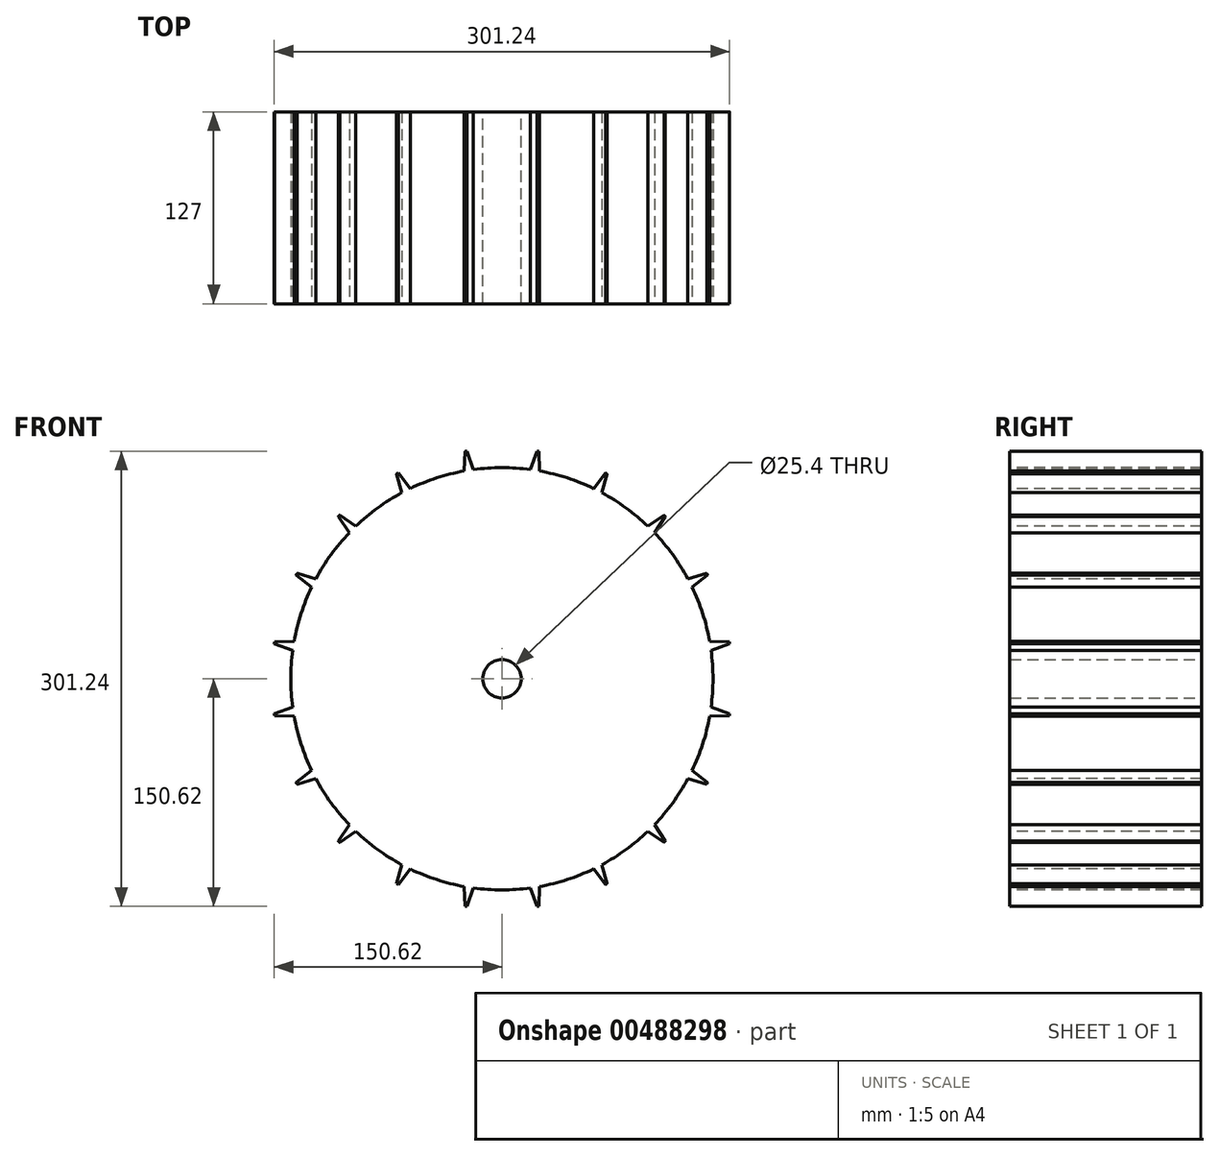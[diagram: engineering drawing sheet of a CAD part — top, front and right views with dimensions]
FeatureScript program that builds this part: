
annotation { "Feature Type Name" : "Feature", "Feature Type Description" : "" }
export const myFeature = defineFeature(function(context is Context, id is Id, definition is map)
    precondition{}
    {
        {
            var Q0;
            Q0=qCreatedBy(makeId("Front.planeOp"),FACE);
            var sketch = newSketch(context, id + "F0", { "sketchPlane" : qUnion([Q0])});
            skCircle(sketch, "E0", {"center": v(0, 0) * mm, "radius": 152.4 * mm});
            skCircle(sketch, "E1", {"center": v(0, 0) * mm, "radius": 76.2 * mm});
            skCircle(sketch, "E2", {"center": v(0, 0) * mm, "radius": 12.7 * mm});
            skSolve(sketch);
        }
        {
            var Q0;
            Q0=makeQuery(id+"F0.imprint","IMPRINT",FACE,{"disambiguationData":[TD([[makeQuery(id+"F0.imprint","IMPRINT",EDGE,{"derivedFrom":sQuery(id+"F0.wireOp",EDGE,"E0")}),1.0]])]});
            var Q1;
            Q1=makeQuery(id+"F0.imprint","IMPRINT",FACE,{"disambiguationData":[TD([[makeQuery(id+"F0.imprint","IMPRINT",EDGE,{"derivedFrom":sQuery(id+"F0.wireOp",EDGE,"E1")}),1.0]])]});
            extrude(context, id + "F1", {"entities" : qUnion([Q0, Q1]), "endBound" : BoundingType.SYMMETRIC, "depth" : 127 * mm});
        }
        {
            var Q0;
            Q0=qCreatedBy(makeId("Front.planeOp"),FACE);
            var sketch = newSketch(context, id + "F2", { "sketchPlane" : qUnion([Q0])});
            skLineSegment(sketch, "E3", {"start": v(0, 0) * mm, "end": v(0, 208.27) * mm, "construction": true});
            skArc(sketch, "E4", {"start": v(18.8, 138.43) * mm, "mid": v(0, 139.7) * mm, "end": v(-18.8, 138.43) * mm});
            skArc(sketch, "E5", {"start": v(23.24, 150.62) * mm, "mid": v(0, 152.4) * mm, "end": v(-23.24, 150.62) * mm});
            skLineSegment(sketch, "E6", {"start": v(18.8, 138.43) * mm, "end": v(23.24, 150.62) * mm});
            skLineSegment(sketch, "E7.MirrorCS", {"start": v(-18.8, 138.43) * mm, "end": v(-23.24, 150.62) * mm});
            skArc(sketch, "E8.1.0", {"start": v(-24.9, 137.46) * mm, "mid": v(-43.17, 132.86) * mm, "end": v(-60.66, 125.84) * mm});
            skLineSegment(sketch, "E8.1.1", {"start": v(-60.66, 125.84) * mm, "end": v(-68.65, 136.06) * mm});
            skArc(sketch, "E8.1.2", {"start": v(-24.44, 150.43) * mm, "mid": v(-47.1, 144.94) * mm, "end": v(-68.65, 136.06) * mm});
            skLineSegment(sketch, "E8.1.3", {"start": v(-24.9, 137.46) * mm, "end": v(-24.44, 150.43) * mm});
            skArc(sketch, "E8.2.0", {"start": v(-66.15, 123.05) * mm, "mid": v(-82.11, 113.02) * mm, "end": v(-96.58, 100.94) * mm});
            skLineSegment(sketch, "E8.2.1", {"start": v(-96.58, 100.94) * mm, "end": v(-107.33, 108.19) * mm});
            skArc(sketch, "E8.2.2", {"start": v(-69.73, 135.51) * mm, "mid": v(-89.58, 123.3) * mm, "end": v(-107.33, 108.19) * mm});
            skLineSegment(sketch, "E8.2.3", {"start": v(-66.15, 123.05) * mm, "end": v(-69.73, 135.51) * mm});
            skArc(sketch, "E8.3.0", {"start": v(-100.94, 96.58) * mm, "mid": v(-113.02, 82.11) * mm, "end": v(-123.05, 66.15) * mm});
            skLineSegment(sketch, "E8.3.1", {"start": v(-123.05, 66.15) * mm, "end": v(-135.51, 69.73) * mm});
            skArc(sketch, "E8.3.2", {"start": v(-108.19, 107.33) * mm, "mid": v(-123.3, 89.58) * mm, "end": v(-135.51, 69.73) * mm});
            skLineSegment(sketch, "E8.3.3", {"start": v(-100.94, 96.58) * mm, "end": v(-108.19, 107.33) * mm});
            skArc(sketch, "E8.4.0", {"start": v(-125.84, 60.66) * mm, "mid": v(-132.86, 43.17) * mm, "end": v(-137.46, 24.9) * mm});
            skLineSegment(sketch, "E8.4.1", {"start": v(-137.46, 24.9) * mm, "end": v(-150.43, 24.44) * mm});
            skArc(sketch, "E8.4.2", {"start": v(-136.06, 68.65) * mm, "mid": v(-144.94, 47.1) * mm, "end": v(-150.43, 24.44) * mm});
            skLineSegment(sketch, "E8.4.3", {"start": v(-125.84, 60.66) * mm, "end": v(-136.06, 68.65) * mm});
            skArc(sketch, "E8.5.0", {"start": v(-138.43, 18.8) * mm, "mid": v(-139.7, 0) * mm, "end": v(-138.43, -18.8) * mm});
            skLineSegment(sketch, "E8.5.1", {"start": v(-138.43, -18.8) * mm, "end": v(-150.62, -23.24) * mm});
            skArc(sketch, "E8.5.2", {"start": v(-150.62, 23.24) * mm, "mid": v(-152.4, 0) * mm, "end": v(-150.62, -23.24) * mm});
            skLineSegment(sketch, "E8.5.3", {"start": v(-138.43, 18.8) * mm, "end": v(-150.62, 23.24) * mm});
            skArc(sketch, "E8.6.0", {"start": v(-137.46, -24.9) * mm, "mid": v(-132.86, -43.17) * mm, "end": v(-125.84, -60.66) * mm});
            skLineSegment(sketch, "E8.6.1", {"start": v(-125.84, -60.66) * mm, "end": v(-136.06, -68.65) * mm});
            skArc(sketch, "E8.6.2", {"start": v(-150.43, -24.44) * mm, "mid": v(-144.94, -47.1) * mm, "end": v(-136.06, -68.65) * mm});
            skLineSegment(sketch, "E8.6.3", {"start": v(-137.46, -24.9) * mm, "end": v(-150.43, -24.44) * mm});
            skArc(sketch, "E8.7.0", {"start": v(-123.05, -66.15) * mm, "mid": v(-113.02, -82.11) * mm, "end": v(-100.94, -96.58) * mm});
            skLineSegment(sketch, "E8.7.1", {"start": v(-100.94, -96.58) * mm, "end": v(-108.19, -107.33) * mm});
            skArc(sketch, "E8.7.2", {"start": v(-135.51, -69.73) * mm, "mid": v(-123.3, -89.58) * mm, "end": v(-108.19, -107.33) * mm});
            skLineSegment(sketch, "E8.7.3", {"start": v(-123.05, -66.15) * mm, "end": v(-135.51, -69.73) * mm});
            skArc(sketch, "E8.8.0", {"start": v(-96.58, -100.94) * mm, "mid": v(-82.11, -113.02) * mm, "end": v(-66.15, -123.05) * mm});
            skLineSegment(sketch, "E8.8.1", {"start": v(-66.15, -123.05) * mm, "end": v(-69.73, -135.51) * mm});
            skArc(sketch, "E8.8.2", {"start": v(-107.33, -108.19) * mm, "mid": v(-89.58, -123.3) * mm, "end": v(-69.73, -135.51) * mm});
            skLineSegment(sketch, "E8.8.3", {"start": v(-96.58, -100.94) * mm, "end": v(-107.33, -108.19) * mm});
            skArc(sketch, "E8.9.0", {"start": v(-60.66, -125.84) * mm, "mid": v(-43.17, -132.86) * mm, "end": v(-24.9, -137.46) * mm});
            skLineSegment(sketch, "E8.9.1", {"start": v(-24.9, -137.46) * mm, "end": v(-24.44, -150.43) * mm});
            skArc(sketch, "E8.9.2", {"start": v(-68.65, -136.06) * mm, "mid": v(-47.1, -144.94) * mm, "end": v(-24.44, -150.43) * mm});
            skLineSegment(sketch, "E8.9.3", {"start": v(-60.66, -125.84) * mm, "end": v(-68.65, -136.06) * mm});
            skArc(sketch, "E8.10.0", {"start": v(-18.8, -138.43) * mm, "mid": v(0, -139.7) * mm, "end": v(18.8, -138.43) * mm});
            skLineSegment(sketch, "E8.10.1", {"start": v(18.8, -138.43) * mm, "end": v(23.24, -150.62) * mm});
            skArc(sketch, "E8.10.2", {"start": v(-23.24, -150.62) * mm, "mid": v(0, -152.4) * mm, "end": v(23.24, -150.62) * mm});
            skLineSegment(sketch, "E8.10.3", {"start": v(-18.8, -138.43) * mm, "end": v(-23.24, -150.62) * mm});
            skArc(sketch, "E8.11.0", {"start": v(24.9, -137.46) * mm, "mid": v(43.17, -132.86) * mm, "end": v(60.66, -125.84) * mm});
            skLineSegment(sketch, "E8.11.1", {"start": v(60.66, -125.84) * mm, "end": v(68.65, -136.06) * mm});
            skArc(sketch, "E8.11.2", {"start": v(24.44, -150.43) * mm, "mid": v(47.1, -144.94) * mm, "end": v(68.65, -136.06) * mm});
            skLineSegment(sketch, "E8.11.3", {"start": v(24.9, -137.46) * mm, "end": v(24.44, -150.43) * mm});
            skArc(sketch, "E8.12.0", {"start": v(66.15, -123.05) * mm, "mid": v(82.11, -113.02) * mm, "end": v(96.58, -100.94) * mm});
            skLineSegment(sketch, "E8.12.1", {"start": v(96.58, -100.94) * mm, "end": v(107.33, -108.19) * mm});
            skArc(sketch, "E8.12.2", {"start": v(69.73, -135.51) * mm, "mid": v(89.58, -123.3) * mm, "end": v(107.33, -108.19) * mm});
            skLineSegment(sketch, "E8.12.3", {"start": v(66.15, -123.05) * mm, "end": v(69.73, -135.51) * mm});
            skArc(sketch, "E8.13.0", {"start": v(100.94, -96.58) * mm, "mid": v(113.02, -82.11) * mm, "end": v(123.05, -66.15) * mm});
            skLineSegment(sketch, "E8.13.1", {"start": v(123.05, -66.15) * mm, "end": v(135.51, -69.73) * mm});
            skArc(sketch, "E8.13.2", {"start": v(108.19, -107.33) * mm, "mid": v(123.3, -89.58) * mm, "end": v(135.51, -69.73) * mm});
            skLineSegment(sketch, "E8.13.3", {"start": v(100.94, -96.58) * mm, "end": v(108.19, -107.33) * mm});
            skArc(sketch, "E8.14.0", {"start": v(125.84, -60.66) * mm, "mid": v(132.86, -43.17) * mm, "end": v(137.46, -24.9) * mm});
            skLineSegment(sketch, "E8.14.1", {"start": v(137.46, -24.9) * mm, "end": v(150.43, -24.44) * mm});
            skArc(sketch, "E8.14.2", {"start": v(136.06, -68.65) * mm, "mid": v(144.94, -47.1) * mm, "end": v(150.43, -24.44) * mm});
            skLineSegment(sketch, "E8.14.3", {"start": v(125.84, -60.66) * mm, "end": v(136.06, -68.65) * mm});
            skArc(sketch, "E8.15.0", {"start": v(138.43, -18.8) * mm, "mid": v(139.7, 0) * mm, "end": v(138.43, 18.8) * mm});
            skLineSegment(sketch, "E8.15.1", {"start": v(138.43, 18.8) * mm, "end": v(150.62, 23.24) * mm});
            skArc(sketch, "E8.15.2", {"start": v(150.62, -23.24) * mm, "mid": v(152.4, 0) * mm, "end": v(150.62, 23.24) * mm});
            skLineSegment(sketch, "E8.15.3", {"start": v(138.43, -18.8) * mm, "end": v(150.62, -23.24) * mm});
            skArc(sketch, "E8.16.0", {"start": v(137.46, 24.9) * mm, "mid": v(132.86, 43.17) * mm, "end": v(125.84, 60.66) * mm});
            skLineSegment(sketch, "E8.16.1", {"start": v(125.84, 60.66) * mm, "end": v(136.06, 68.65) * mm});
            skArc(sketch, "E8.16.2", {"start": v(150.43, 24.44) * mm, "mid": v(144.94, 47.1) * mm, "end": v(136.06, 68.65) * mm});
            skLineSegment(sketch, "E8.16.3", {"start": v(137.46, 24.9) * mm, "end": v(150.43, 24.44) * mm});
            skArc(sketch, "E8.17.0", {"start": v(123.05, 66.15) * mm, "mid": v(113.02, 82.11) * mm, "end": v(100.94, 96.58) * mm});
            skLineSegment(sketch, "E8.17.1", {"start": v(100.94, 96.58) * mm, "end": v(108.19, 107.33) * mm});
            skArc(sketch, "E8.17.2", {"start": v(135.51, 69.73) * mm, "mid": v(123.3, 89.58) * mm, "end": v(108.19, 107.33) * mm});
            skLineSegment(sketch, "E8.17.3", {"start": v(123.05, 66.15) * mm, "end": v(135.51, 69.73) * mm});
            skArc(sketch, "E8.18.0", {"start": v(96.58, 100.94) * mm, "mid": v(82.11, 113.02) * mm, "end": v(66.15, 123.05) * mm});
            skLineSegment(sketch, "E8.18.1", {"start": v(66.15, 123.05) * mm, "end": v(69.73, 135.51) * mm});
            skArc(sketch, "E8.18.2", {"start": v(107.33, 108.19) * mm, "mid": v(89.58, 123.3) * mm, "end": v(69.73, 135.51) * mm});
            skLineSegment(sketch, "E8.18.3", {"start": v(96.58, 100.94) * mm, "end": v(107.33, 108.19) * mm});
            skArc(sketch, "E8.19.0", {"start": v(60.66, 125.84) * mm, "mid": v(43.17, 132.86) * mm, "end": v(24.9, 137.46) * mm});
            skLineSegment(sketch, "E8.19.1", {"start": v(24.9, 137.46) * mm, "end": v(24.44, 150.43) * mm});
            skArc(sketch, "E8.19.2", {"start": v(68.65, 136.06) * mm, "mid": v(47.1, 144.94) * mm, "end": v(24.44, 150.43) * mm});
            skLineSegment(sketch, "E8.19.3", {"start": v(60.66, 125.84) * mm, "end": v(68.65, 136.06) * mm});
            skSolve(sketch);
        }
        {
            var Q0;
            Q0 = qSketchRegion(id + "F2", true);
            extrude(context, id + "F3", {"entities" : qUnion([Q0]), "operationType" : NewBodyOperationType.REMOVE, "endBound" : BoundingType.SYMMETRIC, "oppositeDirection" : true, "depth" : 127 * mm});
        }
    });
